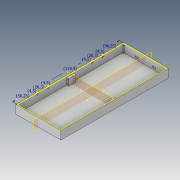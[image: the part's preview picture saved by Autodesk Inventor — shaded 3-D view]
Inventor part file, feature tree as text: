
AUTODESK INVENTOR PART (.ipt)
format: ipt  version: 2019 (Build 230136000, 136)  size: 268,288 bytes
history: native  units: mm
features: sketch x12, extrude x7, hole x4, plane x2, mirror x1, projected_geometry x1
ambient origin geometry x8: Origin, YZ Plane, XZ Plane, XY Plane, X Axis, Y Axis, Z Axis, Center Point
bodies: Solid1 (feature_tree)
feature tree (27):
  sketch  "Sketch1"  dims[d0=295.0mm d1=105.0mm]
  sketch  "Sketch2"  dims[d2=7.6mm d3=3.0mm]
  extrude  "Extrusion1"  Depth=295.0mm
  extrude  "Extrusion2"  Depth=3.0mm
  extrude  "Extrusion4"  Depth=1.0mm TaperAngle=0.0deg
  extrude  "Extrusion6"  Depth=1.0mm
  plane  "Work Plane2"
  plane  "Work Plane4"
  hole  "Hole3"  [1 undecoded]
  hole  "Hole4"  [1 undecoded]
  hole  "Hole5"  [1 undecoded]
  hole  "Hole6"  [1 undecoded]
  mirror  "Mirror6"
  extrude  "Extrusion14"  TaperAngle=150.0deg  [1 undecoded]
  extrude  "Extrusion15"  Depth=4.0mm
  extrude  "Extrusion16"  Depth=4.0mm
  sketch  "Sketch27"  dims[d75=1.5mm d76=60.0mm d77=60.0mm d106=10.0mm d107=10.0mm d108=3.5mm d110=2.6mm d111=6.0mm d112=5.0mm d113=2.0mm d114=14.3117mm d115=5.0mm d116=0.0mm d117=2.6mm d118=6.0mm d119=5.0mm d120=2.0mm d121=14.3117mm d122=15.0mm d123=20.594885mm d124=3.5mm d125=5.0mm d126=2.6mm d127=6.0mm d128=5.0mm d129=2.0mm d130=14.3117mm d131=5.0mm d132=0.0mm d133=2.6mm d134=6.0mm d135=5.0mm d136=2.0mm d137=14.3117mm d138=15.0mm d139=20.594885mm d144=5.0mm d145=5.0mm d148=151.5mm d149=151.5mm d159=4.0mm d160=4.0mm d161=2.2mm d162=2.0mm d163=2.0mm d164=4.0mm d165=4.0mm d166=2.2mm d167=2.0mm d168=2.0mm d169=4.0mm d170=4.0mm d171=2.2mm d172=2.0mm d173=2.0mm d174=4.0mm d175=4.0mm d176=2.2mm d177=2.0mm d178=2.0mm d179=19.0mm d180=0.0mm d181=9.0mm d182=5.0mm d183=4.0mm d184=30.0mm d185=20.0mm d186=0.0mm d187=9.0mm d188=5.0mm d189=40.0mm d190=4.0mm d191=20.0mm d192=0.0mm d193=19.0mm d194=5.0mm d196=56.25mm d197=4.5mm d198=26.3mm d199=4.5mm d200=119.9mm d201=4.5mm d202=26.3mm d203=4.5mm d204=56.25mm d91=1.0mm d92=1.0mm d93=1.0mm d94=0.15mm d95=0.25mm d96=0.375mm d97=14.3117mm d98=0.75mm d99=20.594885mm d100=0.0625mm d101=0.75mm d102=0.375mm]
  sketch  "Sketch5"  dims[d4=14.0mm d7=1.0mm d8=0.0mm]
  sketch  "Sketch7"  dims[d9=23.0mm d10=1.0mm d11=0.0mm d12=0.0mm d35=4.5mm]
  projected_geometry  "Projected Loop4"
  sketch  "Sketch16"  dims[d37=4.5mm d39=4.5mm]
  sketch  "Sketch17"  dims[d40=0.0mm d41=30.8mm]
  sketch  "Sketch18"  dims[d45=4.5mm d46=0.0mm]
  sketch  "Sketch19"  dims[d47=30.8mm d50=10.0mm d51=0.0mm]
  sketch  "Sketch23"  dims[d57=135.0deg d58=135.0deg d61=6.0mm d62=0.0mm d64=150.0deg d65=150.0deg]
  sketch  "Sketch24"  dims[d71=10.0mm d72=4.0mm]
  sketch  "Sketch25"  dims[d73=10.0mm d74=4.0mm]
note: 5 required parameter values undecoded (feature->parameter linkage not recoverable at this tier; creation-order binding heuristic only, values carry confidence <= 0.55)
